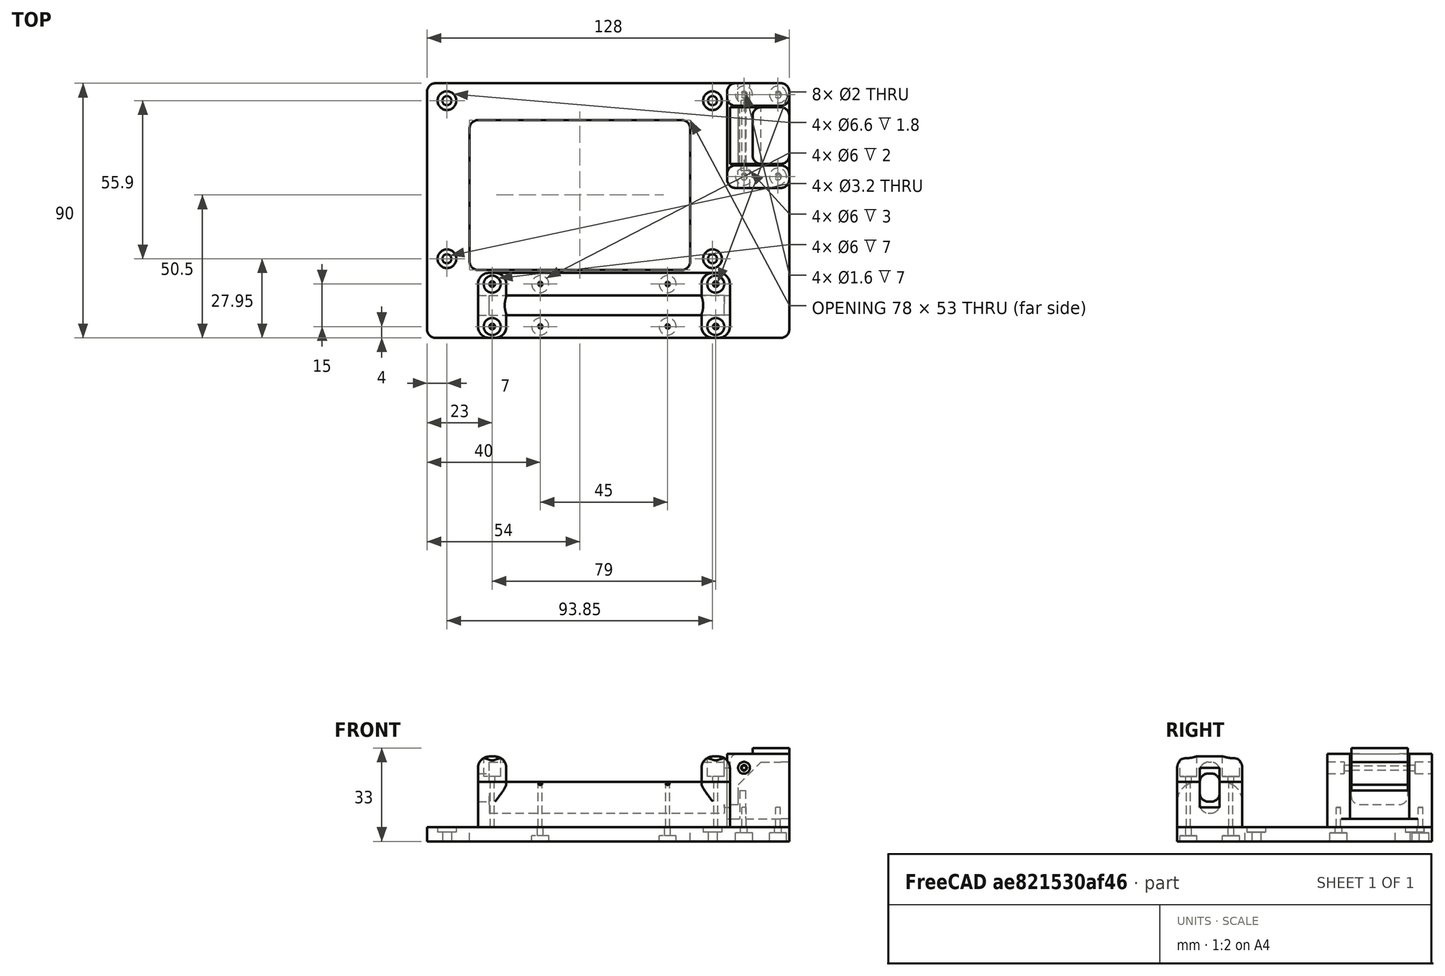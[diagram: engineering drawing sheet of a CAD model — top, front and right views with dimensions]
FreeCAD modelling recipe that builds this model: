
FCSTD DOCUMENT  (FreeCAD 0.19R)
Label: OPI5_Case
License: All rights reserved
LicenseURL: http://en.wikipedia.org/wiki/All_rights_reserved
objects: Part::Cylinder×45, Part::Box×15, Part::Fillet×15, Part::MultiFuse×14, Part::Cut×11, Part::Feature×3, Part::Chamfer×1
note: 104 computed .brp shape members not serialized (recipe doc carries the construction recipe); baked Part::Feature solids carry a one-line shape summary decoded from their .brp

FEATURE [Part::Box] Box017  label="Cube010"
  AttacherType = Attacher::AttachEngine3D
  Height = 5
  Length = 128
  Placement = pos=(-70,-10,0) rot=(0,0,1;0rad)
  Width = 90
FEATURE [Part::Fillet] Fillet002014  label="BaseBottom"
  Base = -> Box017
  Edges = 4 edges r=3: [Edge1,Edge3,Edge5,Edge7]
FEATURE [Part::Cylinder] Cylinder012
  Angle = 360
  AttacherType = Attacher::AttachEngine3D
  Height = 6
  Placement = pos=(-47,-27.85,1.2) rot=(1,0,0;0rad)
  Radius = 1.6
FEATURE [Part::Cylinder] Cylinder013
  Angle = 360
  AttacherType = Attacher::AttachEngine3D
  Height = 6
  Placement = pos=(46.85,-27.85,1.2) rot=(1,0,0;0rad)
  Radius = 1.6
FEATURE [Part::Cylinder] Cylinder014  label="Btn"
  Angle = 360
  AttacherType = Attacher::AttachEngine3D
  Height = 4.2
  Placement = pos=(46.85,-15.5,-2.3) rot=(0,1,0;1.5708rad)
  Radius = 1.2
FEATURE [Part::Cylinder] Cylinder015
  Angle = 360
  AttacherType = Attacher::AttachEngine3D
  Height = 6
  Placement = pos=(-47,28.05,1.2) rot=(1,0,0;0rad)
  Radius = 1.6
FEATURE [Part::Cylinder] Cylinder016
  Angle = 360
  AttacherType = Attacher::AttachEngine3D
  Height = 6
  Placement = pos=(46.85,28.05,1.2) rot=(1,0,0;0rad)
  Radius = 1.6
FEATURE [Part::MultiFuse] Fusion014  label="Opi5Holles"
  Placement = pos=(-51,46,7.2) rot=(1,0,0;3.14159rad)
  Shapes = -> [Cylinder014,Cylinder016,Cylinder013,Cylinder012,Cylinder015]
FEATURE [Part::Cylinder] Cylinder017
  Angle = 360
  AttacherType = Attacher::AttachEngine3D
  Height = 2
  Placement = pos=(-47,28.05,2) rot=(1,0,0;0rad)
  Radius = 3.3
FEATURE [Part::Cylinder] Cylinder018
  Angle = 360
  AttacherType = Attacher::AttachEngine3D
  Height = 2
  Placement = pos=(46.85,28.05,2) rot=(1,0,0;0rad)
  Radius = 3.3
FEATURE [Part::Cylinder] Cylinder019
  Angle = 360
  AttacherType = Attacher::AttachEngine3D
  Height = 2
  Placement = pos=(-47,-27.85,2) rot=(1,0,0;0rad)
  Radius = 3.3
FEATURE [Part::Cylinder] Cylinder020
  Angle = 360
  AttacherType = Attacher::AttachEngine3D
  Height = 2
  Placement = pos=(46.85,-27.85,2) rot=(1,0,0;0rad)
  Radius = 3.3
FEATURE [Part::MultiFuse] Fusion015  label="Fastners"
  Placement = pos=(-51,46,7.2) rot=(1,0,0;3.14159rad)
  Shapes = -> [Cylinder018,Cylinder020,Cylinder019,Cylinder017]
FEATURE [Part::MultiFuse] Fusion  label="OPI5_FastnerHolles"
  Placement = pos=(35,0,0) rot=(0,0,1;0rad)
  Shapes = -> [Fusion014,Fusion015]
FEATURE [Part::Box] Box030  label="Cube023"
  AttacherType = Attacher::AttachEngine3D
  Height = 26
  Length = 22
  Placement = pos=(36,43,5) rot=(0,0,1;0rad)
  Width = 37
FEATURE [Part::Fillet] Fillet002024
  Base = -> Box030
  Edges = 4 edges r=3: [Edge1,Edge3,Edge5,Edge7]
FEATURE [Part::Cylinder] Cylinder026  label="ScrewHolle007"
  Angle = 360
  AttacherType = Attacher::AttachEngine3D
  Height = 12
  Placement = pos=(42,47,0) rot=(0,0,1;0rad)
  Radius = 0.8
FEATURE [Part::Cylinder] Cylinder027  label="ScrewHolle008"
  Angle = 360
  AttacherType = Attacher::AttachEngine3D
  Height = 12
  Placement = pos=(54,47,0) rot=(0,0,1;0rad)
  Radius = 0.8
FEATURE [Part::Cylinder] Cylinder028  label="ScrewHolle009"
  Angle = 360
  AttacherType = Attacher::AttachEngine3D
  Height = 12
  Placement = pos=(42,76,0) rot=(0,0,1;0rad)
  Radius = 0.8
FEATURE [Part::Cylinder] Cylinder029  label="ScrewHolle010"
  Angle = 360
  AttacherType = Attacher::AttachEngine3D
  Height = 12
  Placement = pos=(54,76,0) rot=(0,0,1;0rad)
  Radius = 0.8
FEATURE [Part::Box] Box031  label="Cube024"
  AttacherType = Attacher::AttachEngine3D
  Height = 18
  Length = 21
  Placement = pos=(37,51.5,13) rot=(0,0,1;0rad)
  Width = 20
FEATURE [Part::Cylinder] Cylinder030  label="ScrewHolle011"
  Angle = 360
  AttacherType = Attacher::AttachEngine3D
  Height = 12
  Placement = pos=(54,47,0) rot=(0,0,1;0rad)
  Radius = 1.2
FEATURE [Part::Cylinder] Cylinder031  label="ScrewHolle012"
  Angle = 360
  AttacherType = Attacher::AttachEngine3D
  Height = 12
  Placement = pos=(42,47,0) rot=(0,0,1;0rad)
  Radius = 1.2
FEATURE [Part::Cylinder] Cylinder032  label="ScrewHolle013"
  Angle = 360
  AttacherType = Attacher::AttachEngine3D
  Height = 12
  Placement = pos=(54,76,0) rot=(0,0,1;0rad)
  Radius = 1.2
FEATURE [Part::Cylinder] Cylinder033  label="ScrewHolle014"
  Angle = 360
  AttacherType = Attacher::AttachEngine3D
  Height = 12
  Placement = pos=(42,76,0) rot=(0,0,1;0rad)
  Radius = 1.2
FEATURE [Part::Cylinder] Cylinder034  label="ScrewHolle015"
  Angle = 360
  AttacherType = Attacher::AttachEngine3D
  Height = 3
  Placement = pos=(54,47,0) rot=(0,0,1;0rad)
  Radius = 3
FEATURE [Part::Cylinder] Cylinder035  label="ScrewHolle016"
  Angle = 360
  AttacherType = Attacher::AttachEngine3D
  Height = 3
  Placement = pos=(42,47,0) rot=(0,0,1;0rad)
  Radius = 3
FEATURE [Part::Cylinder] Cylinder036  label="ScrewHolle017"
  Angle = 360
  AttacherType = Attacher::AttachEngine3D
  Height = 3
  Placement = pos=(54,76,0) rot=(0,0,1;0rad)
  Radius = 3
FEATURE [Part::Cylinder] Cylinder037  label="ScrewHolle018"
  Angle = 360
  AttacherType = Attacher::AttachEngine3D
  Height = 3
  Placement = pos=(42,76,0) rot=(0,0,1;0rad)
  Radius = 3
FEATURE [Part::Box] Box039  label="Cube032"
  AttacherType = Attacher::AttachEngine3D
  Height = 6
  Length = 78
  Placement = pos=(-55,14,0) rot=(0,0,1;0rad)
  Width = 53
FEATURE [Part::Fillet] Fillet002029  label="CoolingHollow"
  Base = -> Box039
  Edges = 4 edges r=3: [Edge1,Edge3,Edge5,Edge7]
FEATURE [Part::Box] Box040  label="Cube033"
  AttacherType = Attacher::AttachEngine3D
  Height = 18
  Length = 21
  Placement = pos=(40,51.5,10) rot=(0,0,1;0rad)
  Width = 20
FEATURE [Part::Chamfer] Chamfer
  Base = -> Box040
  Edges = 1 edges r=8: [Edge2]
FEATURE [Part::Cylinder] Cylinder038  label="ScrewHolle019"
  Angle = 360
  AttacherType = Attacher::AttachEngine3D
  Height = 30
  Placement = pos=(42,45,26) rot=(-1,0,0;1.5708rad)
  Radius = 0.8
FEATURE [Part::Fillet] Fillet002030
  Base = -> Box031
  Edges = 2 edges r=3: [Edge5,Edge7]
FEATURE [Part::Fillet] Fillet002031
  Base = -> Fillet002030
  Edges = 2 edges r=3: [Edge14,Edge16]
FEATURE [Part::Fillet] Fillet002032
  Base = -> Fillet002031
  Edges = 1 edges r=3: [Edge12]
FEATURE [Part::MultiFuse] Fusion024
  Shapes = -> [Chamfer,Cylinder038]
FEATURE [Part::Box] Box041  label="Cube034"
  AttacherType = Attacher::AttachEngine3D
  Height = 5
  Length = 13
  Placement = pos=(45,51.5,28) rot=(0,0,1;0rad)
  Width = 20
FEATURE [Part::Fillet] Fillet002033
  Base = -> Box041
  Edges = 4 edges r=3: [Edge1,Edge3,Edge5,Edge7]
FEATURE [Part::MultiFuse] Fusion025
  Shapes = -> [Fillet002032,Fillet002033]
FEATURE [Part::Cut] Cut006  label="Button"
  Base = -> Fusion025
  Tool = -> Fusion024
FEATURE [Part::Box] Box042  label="Cube035"
  AttacherType = Attacher::AttachEngine3D
  Height = 28
  Length = 25
  Placement = pos=(35,51,8) rot=(0,0,1;0rad)
  Width = 21
FEATURE [Part::Box] Box043  label="Cube036"
  AttacherType = Attacher::AttachEngine3D
  Height = 13
  Length = 2
  Placement = pos=(40.5,50,5) rot=(0,0,1;0rad)
  Width = 23
FEATURE [Part::Cylinder] Cylinder039  label="ScrewHolle020"
  Angle = 360
  AttacherType = Attacher::AttachEngine3D
  Height = 45
  Placement = pos=(42,40,26) rot=(-1,0,0;1.5708rad)
  Radius = 1
FEATURE [Part::Cylinder] Cylinder040  label="ScrewHolle021"
  Angle = 360
  AttacherType = Attacher::AttachEngine3D
  Height = 8
  Placement = pos=(42,41,26) rot=(-1,0,0;1.5708rad)
  Radius = 2.1
FEATURE [Part::Cylinder] Cylinder041  label="ScrewHolle022"
  Angle = 360
  AttacherType = Attacher::AttachEngine3D
  Height = 8
  Placement = pos=(42,74,26) rot=(-1,0,0;1.5708rad)
  Radius = 2.1
FEATURE [Part::Cut] Cut007
  Base = -> Fillet002024
  Tool = -> Box042
FEATURE [Part::MultiFuse] Fusion028  label="BtnBoxBody"
  Shapes = -> [Cut007,Box043]
FEATURE [Part::MultiFuse] Fusion029
  Shapes = -> [Cylinder026,Cylinder027,Cylinder028,Cylinder029,Cylinder039,Cylinder040,Cylinder041]
FEATURE [Part::Fillet] Fillet002034
  Base = -> Fusion028
  Edges = 4 edges r=3: [Edge14,Edge16,Edge33,Edge35]
FEATURE [Part::Cut] Cut008  label="BtnBox"
  Base = -> Fillet002034
  Tool = -> Fusion029
FEATURE [Part::MultiFuse] Fusion030  label="PushButtonScrewHolles"
  Shapes = -> [Cylinder037,Cylinder030,Cylinder031,Cylinder032,Cylinder033,Cylinder034,Cylinder035,Cylinder036]
FEATURE [Part::MultiFuse] Fusion031
  Shapes = -> [Fillet002029,Fusion,Fusion030]
FEATURE [Part::Cut] Cut
  Base = -> Fillet002014
  Tool = -> Fusion031
FEATURE [Part::Box] Box044  label="Cube037"
  AttacherType = Attacher::AttachEngine3D
  Height = 10
  Length = 83
  Placement = pos=(-50,0,4) rot=(0,0,1;0rad)
  Width = 7
FEATURE [Part::Fillet] Fillet002036
  Base = -> Box044
  Edges = 4 edges r=3: [Edge9,Edge10,Edge11,Edge12]
FEATURE [Part::Box] Box045  label="Cube038"
  AttacherType = Attacher::AttachEngine3D
  Height = 14
  Length = 10
  Placement = pos=(83,0,2) rot=(0,0,1;0rad)
  Width = 7
FEATURE [Part::Box] Box029  label="Cube022"
  AttacherType = Attacher::AttachEngine3D
  Height = 18
  Length = 83
  Width = 7
FEATURE [Part::Fillet] Fillet002035
  Base = -> Box029
  Edges = 4 edges r=3: [Edge9,Edge10,Edge11,Edge12]
FEATURE [Part::Box] Box046  label="Cube039"
  AttacherType = Attacher::AttachEngine3D
  Height = 16
  Length = 89
  Placement = pos=(-52,-10,5) rot=(0,0,1;0rad)
  Width = 23
FEATURE [Part::Fillet] Fillet
  Base = -> Box046
  Edges = 4 edges r=4: [Edge1,Edge3,Edge5,Edge7]
FEATURE [Part::MultiFuse] Fusion032  label="HubHollow"
  Placement = pos=(-48,-2,10) rot=(0,0,1;0rad)
  Shapes = -> [Box045,Fillet002036,Fillet002035]
FEATURE [Part::Cylinder] Cylinder  label="HubScrewHolle001"
  Angle = 360
  AttacherType = Attacher::AttachEngine3D
  Height = 25
  Placement = pos=(-30,-6,0) rot=(0,0,1;0rad)
  Radius = 0.7
FEATURE [Part::Cylinder] Cylinder042  label="HubScrewHolle002"
  Angle = 360
  AttacherType = Attacher::AttachEngine3D
  Height = 25
  Placement = pos=(-30,9,0) rot=(0,0,1;0rad)
  Radius = 0.7
FEATURE [Part::Cylinder] Cylinder043  label="HubScrewHolle003"
  Angle = 360
  AttacherType = Attacher::AttachEngine3D
  Height = 25
  Placement = pos=(15,-6,0) rot=(0,0,1;0rad)
  Radius = 0.7
FEATURE [Part::Cylinder] Cylinder044  label="HubScrewHolle004"
  Angle = 360
  AttacherType = Attacher::AttachEngine3D
  Height = 25
  Placement = pos=(15,9,0) rot=(0,0,1;0rad)
  Radius = 0.7
FEATURE [Part::Cylinder] Cylinder045  label="HubScrewHolle005"
  Angle = 360
  AttacherType = Attacher::AttachEngine3D
  Height = 25
  Placement = pos=(-47,-6,0) rot=(0,0,1;0rad)
  Radius = 0.7
FEATURE [Part::Cylinder] Cylinder046  label="HubScrewHolle006"
  Angle = 360
  AttacherType = Attacher::AttachEngine3D
  Height = 25
  Placement = pos=(-47,9,0) rot=(0,0,1;0rad)
  Radius = 0.7
FEATURE [Part::Cylinder] Cylinder047  label="HubScrewHolle007"
  Angle = 360
  AttacherType = Attacher::AttachEngine3D
  Height = 25
  Placement = pos=(32,9,0) rot=(0,0,1;0rad)
  Radius = 0.7
FEATURE [Part::Cylinder] Cylinder048  label="HubScrewHolle008"
  Angle = 360
  AttacherType = Attacher::AttachEngine3D
  Height = 25
  Placement = pos=(32,-6,0) rot=(0,0,1;0rad)
  Radius = 0.7
FEATURE [Part::MultiFuse] Fusion033
  Shapes = -> [Cylinder048,Cylinder,Cylinder042,Cylinder043,Cylinder044,Cylinder045,Cylinder046,Cylinder047]
FEATURE [Part::MultiFuse] Fusion034
  Shapes = -> [Fusion032,Fusion033]
FEATURE [Part::Cut] Cut009  label="USBHubBottomHolder"
  Base = -> Fillet
  Tool = -> Fusion034
FEATURE [Part::Cylinder] Cylinder050  label="HubScrewHolle010"
  Angle = 360
  AttacherType = Attacher::AttachEngine3D
  Height = 25
  Placement = pos=(-30,-6,0) rot=(0,0,1;0rad)
  Radius = 1
FEATURE [Part::Cylinder] Cylinder051  label="HubScrewHolle011"
  Angle = 360
  AttacherType = Attacher::AttachEngine3D
  Height = 25
  Placement = pos=(-30,9,0) rot=(0,0,1;0rad)
  Radius = 1
FEATURE [Part::Cylinder] Cylinder052  label="HubScrewHolle012"
  Angle = 360
  AttacherType = Attacher::AttachEngine3D
  Height = 25
  Placement = pos=(15,-6,0) rot=(0,0,1;0rad)
  Radius = 1
FEATURE [Part::Cylinder] Cylinder053  label="HubScrewHolle013"
  Angle = 360
  AttacherType = Attacher::AttachEngine3D
  Height = 25
  Placement = pos=(15,9,0) rot=(0,0,1;0rad)
  Radius = 1
FEATURE [Part::Cylinder] Cylinder054  label="HubScrewHolle014"
  Angle = 360
  AttacherType = Attacher::AttachEngine3D
  Height = 25
  Placement = pos=(-47,-6,10) rot=(0,0,1;0rad)
  Radius = 1
FEATURE [Part::Cylinder] Cylinder055  label="HubScrewHolle015"
  Angle = 360
  AttacherType = Attacher::AttachEngine3D
  Height = 25
  Placement = pos=(-47,9,10) rot=(0,0,1;0rad)
  Radius = 1
FEATURE [Part::Cylinder] Cylinder057  label="HubScrewHolle017"
  Angle = 360
  AttacherType = Attacher::AttachEngine3D
  Height = 2
  Placement = pos=(15,-6,0) rot=(0,0,1;0rad)
  Radius = 3
FEATURE [Part::Cylinder] Cylinder058  label="HubScrewHolle018"
  Angle = 360
  AttacherType = Attacher::AttachEngine3D
  Height = 2
  Placement = pos=(-30,-6,0) rot=(0,0,1;0rad)
  Radius = 3
FEATURE [Part::Cylinder] Cylinder059  label="HubScrewHolle019"
  Angle = 360
  AttacherType = Attacher::AttachEngine3D
  Height = 2
  Placement = pos=(-30,9,0) rot=(0,0,1;0rad)
  Radius = 3
FEATURE [Part::Cylinder] Cylinder060  label="HubScrewHolle020"
  Angle = 360
  AttacherType = Attacher::AttachEngine3D
  Height = 2
  Placement = pos=(15,9,0) rot=(0,0,1;0rad)
  Radius = 3
FEATURE [Part::Feature] Fusion032001  label="HubHollow001"
  Placement = pos=(-48,-2,10) rot=(0,0,1;0rad)
  shape: bbox 143 x 7 x 18 mm, 32 faces (baked)
FEATURE [Part::Box] Box047  label="Cube040"
  AttacherType = Attacher::AttachEngine3D
  Height = 9
  Length = 10
  Placement = pos=(-52,-10,21) rot=(0,0,1;0rad)
  Width = 23
FEATURE [Part::Fillet] Fillet002037
  Base = -> Box047
  Edges = 4 edges r=4: [Edge1,Edge3,Edge5,Edge7]
FEATURE [Part::MultiFuse] Fusion032002
  Shapes = -> [Cylinder050,Cylinder051,Cylinder052,Cylinder053,Cylinder057,Cylinder058,Cylinder059,Cylinder060]
FEATURE [Part::Cut] Cut010  label="OPi5Base"
  Base = -> Cut
  Tool = -> Fusion032002
FEATURE [Part::Cylinder] Cylinder061  label="HubScrewHolle021"
  Angle = 360
  AttacherType = Attacher::AttachEngine3D
  Height = 25
  Placement = pos=(-47,-6,23) rot=(0,0,1;0rad)
  Radius = 3
FEATURE [Part::Cylinder] Cylinder062  label="HubScrewHolle022"
  Angle = 360
  AttacherType = Attacher::AttachEngine3D
  Height = 25
  Placement = pos=(-47,9,23) rot=(0,0,1;0rad)
  Radius = 3
FEATURE [Part::MultiFuse] Fusion032003
  Shapes = -> [Cylinder054,Cylinder055,Cylinder061,Cylinder062]
FEATURE [Part::Fillet] Fillet002038
  Base = -> Fillet002037
  Edges = 1 edges r=4: [Edge7]
FEATURE [Part::Cut] Cut011  label="HubCap001"
  Base = -> Fillet002038
  Tool = -> Fusion032003
FEATURE [Part::Feature] Cut011001  label="HubCap002"
  Placement = pos=(79,0,0) rot=(0,0,1;0rad)
  shape: bbox 10 x 23 x 9 mm, 24 faces (baked)
FEATURE [Part::Feature] Fusion032004  label="HubHollow002"
  Placement = pos=(-48,-2,10) rot=(0,0,1;0rad)
  shape: bbox 143 x 7 x 18 mm, 32 faces (baked)
FEATURE [Part::Cut] Cut011002  label="HubCap003"
  Base = -> Cut011
  Tool = -> Fusion032001
FEATURE [Part::Cut] Cut011003  label="HubCap004"
  Base = -> Cut011001
  Tool = -> Fusion032004
FEATURE [Part::Box] Box  label="Cube"
  AttacherType = Attacher::AttachEngine3D
  Height = 21
  Length = 69
  Placement = pos=(-42,-10,0) rot=(0,0,1;0rad)
  Width = 23
FEATURE [Part::Fillet] Fillet002039
  Base = -> Box
  Edges = 2 edges r=7: [Edge10,Edge12]
FEATURE [Part::Box] Box048  label="Cube041"
  AttacherType = Attacher::AttachEngine3D
  Height = 21
  Length = 69
  Placement = pos=(-42,-10,14) rot=(0,0,1;0rad)
  Width = 23
FEATURE [Part::Cut] Cut011004
  Base = -> Box048
  Tool = -> Fillet002039
FEATURE [Part::Cut] Cut011005
  Base = -> Cut009
  Tool = -> Cut011004
FEATURE [Part::Fillet] Fillet002040  label="HubHolder"
  Base = -> Cut011005
  Edges = 4 edges r=4: [Edge57,Edge61,Edge74,Edge76]
